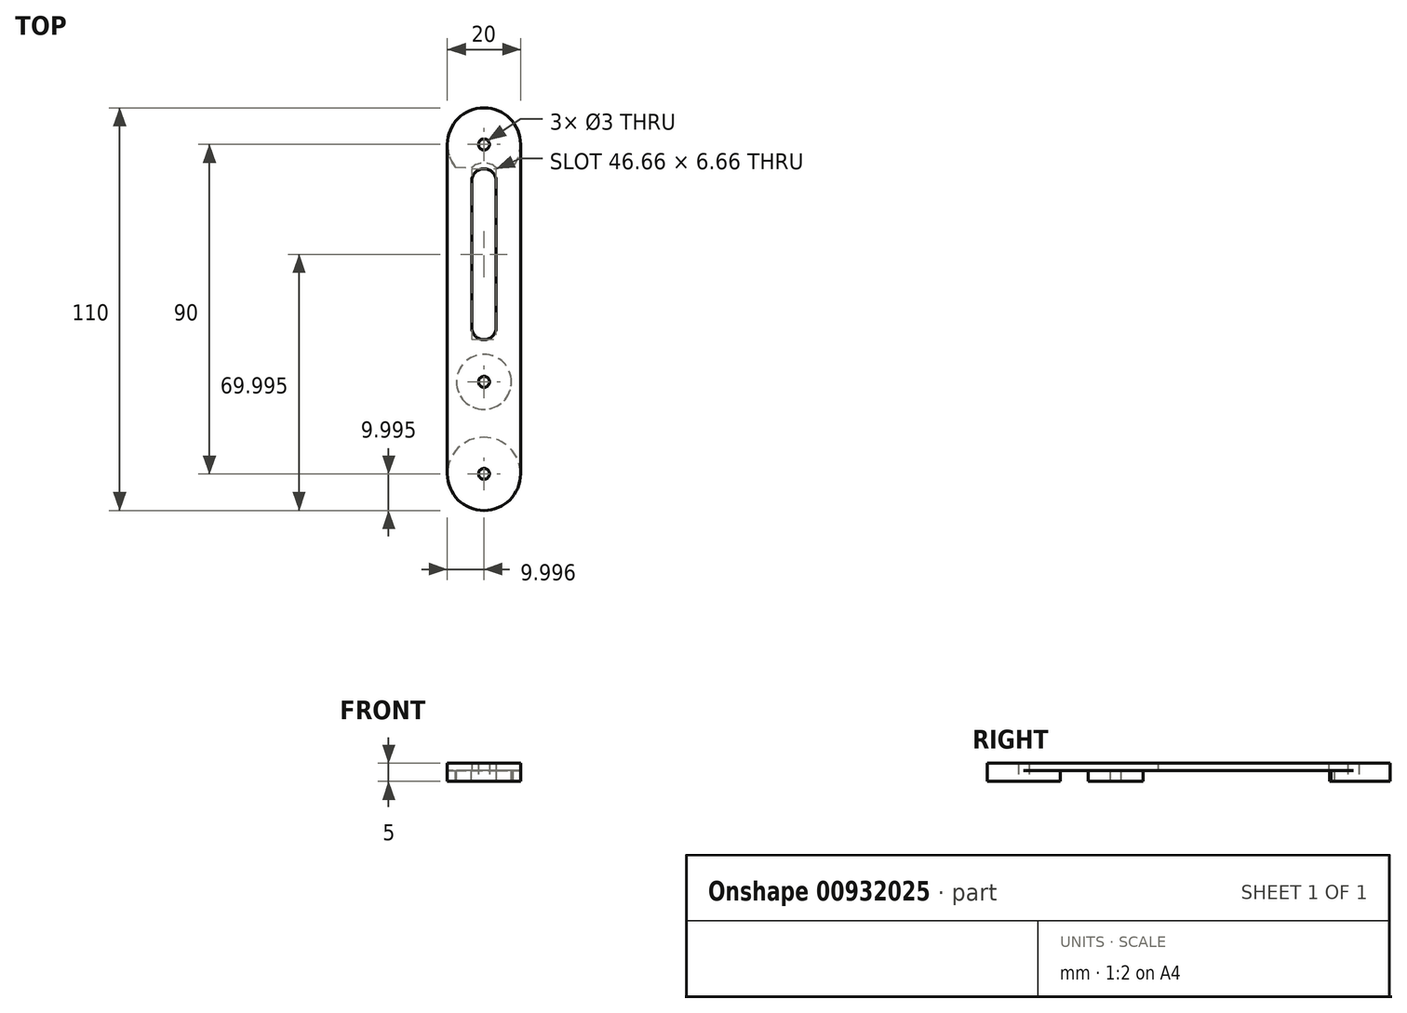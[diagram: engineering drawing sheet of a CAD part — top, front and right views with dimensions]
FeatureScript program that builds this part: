
annotation { "Feature Type Name" : "Feature", "Feature Type Description" : "" }
export const myFeature = defineFeature(function(context is Context, id is Id, definition is map)
    precondition{}
    {
        {
            var Q0;
            Q0=qCreatedBy(makeId("Top.planeOp"),FACE);
            var sketch = newSketch(context, id + "F0", { "sketchPlane" : qUnion([Q0])});
            skLineSegment(sketch, "E0.left", {"start": v(-8.15, 43.4) * mm, "end": v(-8.15, -46.6) * mm});
            skLineSegment(sketch, "E0.right", {"start": v(11.85, 43.4) * mm, "end": v(11.85, -46.6) * mm});
            skArc(sketch, "E1", {"start": v(11.85, 43.4) * mm, "mid": v(1.85, 53.4) * mm, "end": v(-8.15, 43.4) * mm});
            skArc(sketch, "E2", {"start": v(-8.15, -46.6) * mm, "mid": v(1.85, -56.6) * mm, "end": v(11.85, -46.6) * mm});
            skCircle(sketch, "E3", {"center": v(1.85, 43.4) * mm, "radius": 1.5 * mm});
            skCircle(sketch, "E4", {"center": v(1.85, -46.6) * mm, "radius": 1.5 * mm});
            skPoint(sketch, "E5.startSnap0", {"position": v(1.85, 33.4) * mm});
            skLineSegment(sketch, "E6.left", {"start": v(5.18, -6.6) * mm, "end": v(5.18, 33.4) * mm});
            skLineSegment(sketch, "E6.right", {"start": v(-1.48, -6.6) * mm, "end": v(-1.48, 33.4) * mm});
            skPoint(sketch, "E6.middle", {"position": v(1.85, 15.82) * mm});
            skPoint(sketch, "E7.orphan", {"position": v(11.85, 33.4) * mm});
            skPoint(sketch, "E8.orphan", {"position": v(5.18, 38.23) * mm});
            skPoint(sketch, "E9.orphan", {"position": v(-1.48, 38.23) * mm});
            skArc(sketch, "E10", {"start": v(5.18, 33.4) * mm, "mid": v(1.85, 36.73) * mm, "end": v(-1.48, 33.4) * mm});
            skArc(sketch, "E11", {"start": v(-1.48, -6.6) * mm, "mid": v(1.85, -9.93) * mm, "end": v(5.18, -6.6) * mm});
            skSolve(sketch);
        }
        {
            var Q0;
            Q0 = qSketchRegion(id + "F0", true);
            extrude(context, id + "F1", {"entities" : qUnion([Q0]), "depth" : 2 * mm, "offsetDistance" : 25 * mm});
        }
        {
            var Q0;
            Q0=makeQuery(id+"F1.opExtrude","CAP_FACE",FACE,{"disambiguationData":[OSD([sQuery(id+"F0.wireOp",EDGE,"E0.left"),sQuery(id+"F0.wireOp",EDGE,"E0.right"),sQuery(id+"F0.wireOp",EDGE,"E1"),sQuery(id+"F0.wireOp",EDGE,"E2"),sQuery(id+"F0.wireOp",EDGE,"E3"),sQuery(id+"F0.wireOp",EDGE,"E4"),sQuery(id+"F0.wireOp",EDGE,"E6.left"),sQuery(id+"F0.wireOp",EDGE,"E6.right"),sQuery(id+"F0.wireOp",EDGE,"E10"),sQuery(id+"F0.wireOp",EDGE,"E11")])],"isStart":true});
            var sketch = newSketch(context, id + "F2", { "sketchPlane" : qUnion([Q0])});
            skArc(sketch, "E12", {"start": v(11.85, -43.4) * mm, "mid": v(10.44, -38.29) * mm, "end": v(6.63, -34.61) * mm});
            skArc(sketch, "E13", {"start": v(-2.94, -34.61) * mm, "mid": v(1.85, -38.33) * mm, "end": v(6.63, -34.61) * mm});
            skArc(sketch, "E14", {"start": v(-8.15, -43.4) * mm, "mid": v(1.85, -53.4) * mm, "end": v(11.85, -43.4) * mm});
            skPoint(sketch, "E15.trimOffspring.end.orphan", {"position": v(1.85, -28.12) * mm});
            skArc(sketch, "E16.trimOffspring", {"start": v(-2.94, -34.61) * mm, "mid": v(-6.75, -38.29) * mm, "end": v(-8.15, -43.4) * mm});
            skSolve(sketch);
        }
        {
            var Q0;
            Q0=makeQuery(id+"F2.imprint","IMPRINT",FACE,{"disambiguationData":[TD([[makeQuery(id+"F2.imprint","IMPRINT",EDGE,{"derivedFrom":sQuery(id+"F2.wireOp",EDGE,"E12")}),1.0]])]});
            extrude(context, id + "F3", {"entities" : qUnion([Q0]), "operationType" : NewBodyOperationType.ADD, "depth" : 3 * mm, "offsetDistance" : 25 * mm});
        }
        {
            var Q0;
            Q0=makeQuery(id+"F3.opExtrude","SWEPT_EDGE",EDGE,{"disambiguationData":[OSD([sQuery(id+"F2.wireOp",EDGE,"E13"),sQuery(id+"F2.wireOp",EDGE,"E16.trimOffspring")])]});
            chamfer(context, id + "F4", {"entities" : qUnion([Q0]), "width" : 3 * mm, "tangentPropagation" : true});
        }
        {
            var Q0;
            Q0=makeQuery(id+"F3.opExtrude","SWEPT_EDGE",EDGE,{"disambiguationData":[OSD([sQuery(id+"F2.wireOp",EDGE,"E12"),sQuery(id+"F2.wireOp",EDGE,"E13")])]});
            chamfer(context, id + "F5", {"entities" : qUnion([Q0]), "width" : 3 * mm, "tangentPropagation" : true});
        }
        {
            var Q0;
            Q0=makeQuery(id+"F1.opExtrude","CAP_FACE",FACE,{"disambiguationData":[OSD([sQuery(id+"F0.wireOp",EDGE,"E0.left"),sQuery(id+"F0.wireOp",EDGE,"E0.right"),sQuery(id+"F0.wireOp",EDGE,"E1"),sQuery(id+"F0.wireOp",EDGE,"E2"),sQuery(id+"F0.wireOp",EDGE,"E3"),sQuery(id+"F0.wireOp",EDGE,"E4"),sQuery(id+"F0.wireOp",EDGE,"E6.left"),sQuery(id+"F0.wireOp",EDGE,"E6.right"),sQuery(id+"F0.wireOp",EDGE,"E10"),sQuery(id+"F0.wireOp",EDGE,"E11")])],"isStart":true});
            var sketch = newSketch(context, id + "F6", { "sketchPlane" : qUnion([Q0])});
            skPoint(sketch, "E17.end.orphan", {"position": v(1.85, 56.6) * mm});
            skPoint(sketch, "E17.start.orphan", {"position": v(1.85, 46.6) * mm});
            skArc(sketch, "E18", {"start": v(-8.15, 46.6) * mm, "mid": v(1.85, 36.6) * mm, "end": v(11.85, 46.6) * mm});
            skSolve(sketch);
        }
        {
            var Q0;
            Q0=makeQuery(id+"F6.imprint","IMPRINT",FACE,{"disambiguationData":[TD([[makeQuery(id+"F6.imprint","IMPRINT",EDGE,{"derivedFrom":sQuery(id+"F6.wireOp",EDGE,"E18")}),1.0]])]});
            extrude(context, id + "F7", {"entities" : qUnion([Q0]), "operationType" : NewBodyOperationType.ADD, "depth" : 3 * mm, "offsetDistance" : 25 * mm});
        }
        {
            var Q0;
            Q0=makeQuery(id+"F1.opExtrude","CAP_FACE",FACE,{"disambiguationData":[OSD([sQuery(id+"F0.wireOp",EDGE,"E0.left"),sQuery(id+"F0.wireOp",EDGE,"E0.right"),sQuery(id+"F0.wireOp",EDGE,"E1"),sQuery(id+"F0.wireOp",EDGE,"E2"),sQuery(id+"F0.wireOp",EDGE,"E3"),sQuery(id+"F0.wireOp",EDGE,"E4"),sQuery(id+"F0.wireOp",EDGE,"E6.left"),sQuery(id+"F0.wireOp",EDGE,"E6.right"),sQuery(id+"F0.wireOp",EDGE,"E10"),sQuery(id+"F0.wireOp",EDGE,"E11")])],"isStart":false});
            var sketch = newSketch(context, id + "F8", { "sketchPlane" : qUnion([Q0])});
            skLineSegment(sketch, "E19", {"start": v(-8.15, -46.6) * mm, "end": v(11.85, -46.6) * mm});
            skArc(sketch, "E20", {"start": v(11.85, -46.6) * mm, "mid": v(1.85, -36.6) * mm, "end": v(-8.15, -46.6) * mm});
            skLineSegment(sketch, "E21", {"start": v(1.85, -46.6) * mm, "end": v(1.85, -36.6) * mm});
            skPoint(sketch, "E21.endSnap0", {"position": v(1.85, -9.93) * mm});
            skCircle(sketch, "E22", {"center": v(1.85, -21.47) * mm, "radius": 1.5 * mm});
            skPoint(sketch, "E23.orphan", {"position": v(1.85, -11.53) * mm});
            skSolve(sketch);
        }
        {
            var Q0;
            Q0=makeQuery(id+"F8.imprint","IMPRINT",FACE,{"disambiguationData":[TD([[makeQuery(id+"F8.imprint","IMPRINT",EDGE,{"derivedFrom":sQuery(id+"F8.wireOp",EDGE,"E22")}),1.0]])]});
            extrude(context, id + "F9", {"entities" : qUnion([Q0]), "operationType" : NewBodyOperationType.REMOVE, "oppositeDirection" : true, "depth" : 5 * mm, "offsetDistance" : 25 * mm});
        }
        {
            var Q0;
            Q0=makeQuery(id+"F1.opExtrude","CAP_FACE",FACE,{"disambiguationData":[OSD([sQuery(id+"F0.wireOp",EDGE,"E0.left"),sQuery(id+"F0.wireOp",EDGE,"E0.right"),sQuery(id+"F0.wireOp",EDGE,"E1"),sQuery(id+"F0.wireOp",EDGE,"E2"),sQuery(id+"F0.wireOp",EDGE,"E3"),sQuery(id+"F0.wireOp",EDGE,"E4"),sQuery(id+"F0.wireOp",EDGE,"E6.left"),sQuery(id+"F0.wireOp",EDGE,"E6.right"),sQuery(id+"F0.wireOp",EDGE,"E10"),sQuery(id+"F0.wireOp",EDGE,"E11")])],"isStart":true});
            var sketch = newSketch(context, id + "F10", { "sketchPlane" : qUnion([Q0])});
            skCircle(sketch, "E24", {"center": v(1.85, 21.47) * mm, "radius": 7.5 * mm});
            skSolve(sketch);
        }
        {
            var Q0;
            Q0=makeQuery(id+"F10.imprint","IMPRINT",FACE,{"disambiguationData":[TD([[makeQuery(id+"F10.imprint","IMPRINT",EDGE,{"derivedFrom":sQuery(id+"F10.wireOp",EDGE,"E24")}),1.0]])]});
            extrude(context, id + "F11", {"entities" : qUnion([Q0]), "operationType" : NewBodyOperationType.ADD, "depth" : 3 * mm, "offsetDistance" : 25 * mm});
        }
    });
